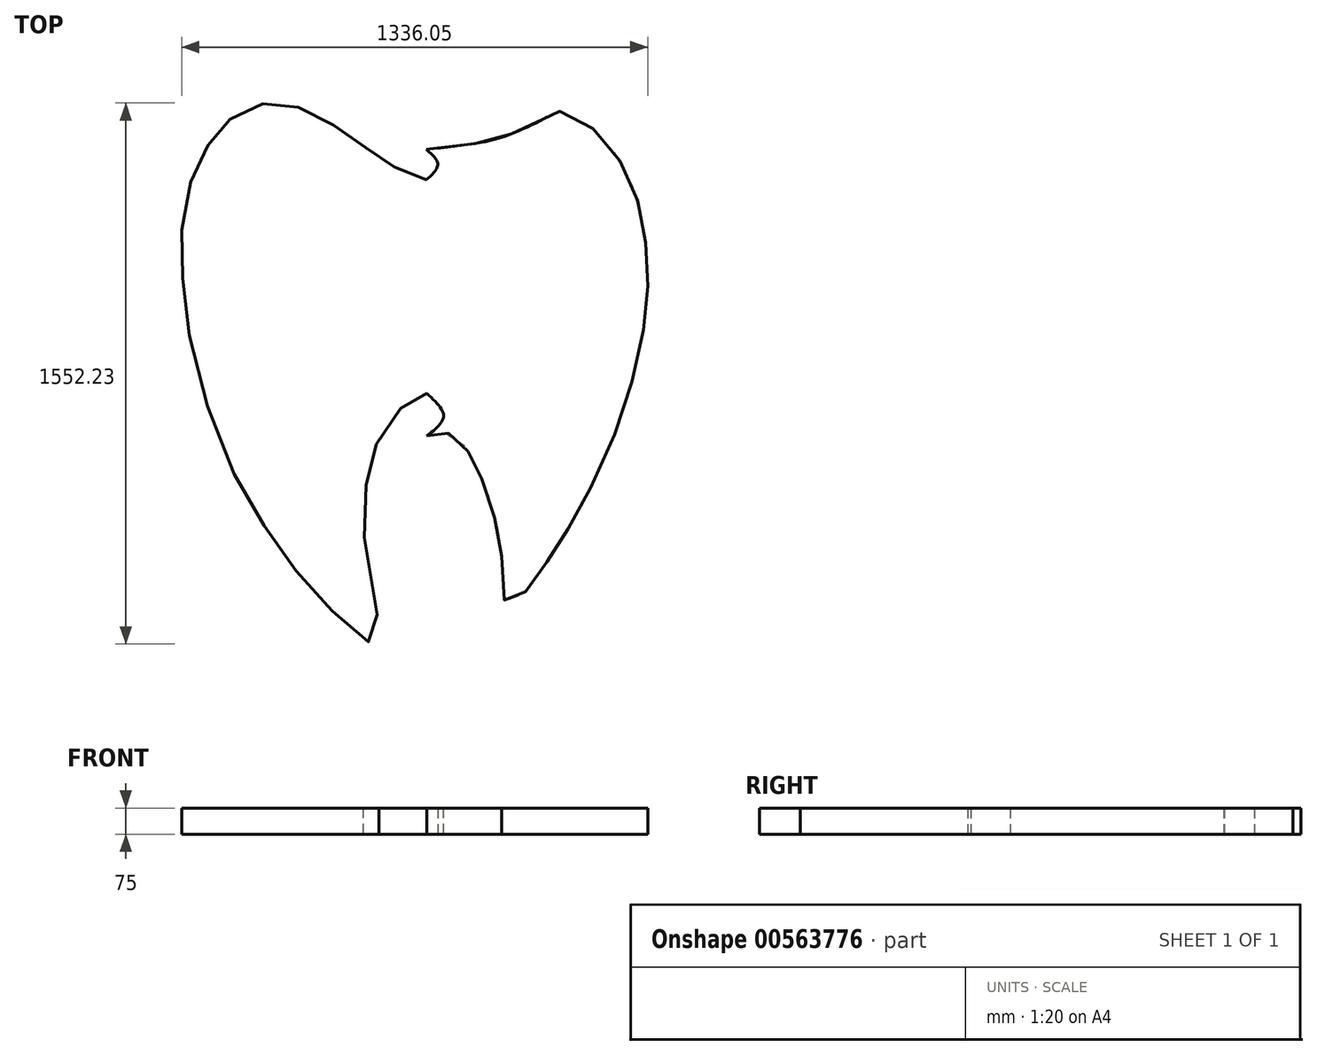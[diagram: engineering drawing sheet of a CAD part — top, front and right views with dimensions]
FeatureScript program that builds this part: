
annotation { "Feature Type Name" : "Feature", "Feature Type Description" : "" }
export const myFeature = defineFeature(function(context is Context, id is Id, definition is map)
    precondition{}
    {
        {
            var Q0;
            Q0=qCreatedBy(makeId("Top.planeOp"),FACE);
            var sketch = newSketch(context, id + "F0", { "sketchPlane" : qUnion([Q0])});
            skFitSpline(sketch, "E0", {"points": [v(131.96, -83.23) * mm, v(71.7, -58) * mm, v(9.47, -61.65) * mm, v(-42.11, -91.08) * mm, v(-114.72, -186.11) * mm, v(-148.68, -304.12) * mm, v(-156, -483.6) * mm, v(-121, -773.99) * mm, v(-175.45, -749.35) * mm, v(-306.38, -623.6) * mm, v(-428.24, -462.85) * mm, v(-551.4, -245.06) * mm, v(-659, 106.26) * mm, v(-679.74, 314.98) * mm, v(-674.56, 467.95) * mm, v(-629.18, 611.85) * mm, v(-586.4, 680.55) * mm, v(-526.77, 740.19) * mm, v(-445.1, 772.6) * mm, v(-358.24, 766.12) * mm, v(-270.09, 725.93) * mm, v(-172.86, 661.1) * mm, v(-115.82, 617.03) * mm, v(-31.55, 571.66) * mm, v(55.3, 550.92) * mm, v(199.2, 557.4) * mm, v(197.9, 557.4) * mm], "startDerivative": vector(-2057.54, 1113.53) * mm, "endDerivative": vector(-522.46, -16.62) * mm});
            skLineSegment(sketch, "E1", {"start": v(-24.8, 1210.26) * mm, "end": v(-24.8, -999.05) * mm, "construction": true});
            skLineSegment(sketch, "E2", {"start": v(199.2, 557.4) * mm, "end": v(131.96, -83.23) * mm});
            skSolve(sketch);
        }
        {
            var Q0;
            Q0=qCreatedBy(makeId("Top.planeOp"),FACE);
            var sketch = newSketch(context, id + "F1", { "sketchPlane" : qUnion([Q0])});
            skFitSpline(sketch, "E3", {"points": [v(21.78, -180.5) * mm, v(51.11, -172.25) * mm, v(86.86, -174.08) * mm, v(124.45, -203.42) * mm, v(155.61, -256.58) * mm, v(185.86, -320.75) * mm, v(222.53, -439) * mm, v(236.28, -543.5) * mm, v(249.12, -658.09) * mm, v(287.62, -644.34) * mm, v(329.78, -593.92) * mm, v(395.78, -496.75) * mm, v(449.87, -406.92) * mm, v(543.37, -218.08) * mm, v(613.04, -13.66) * mm, v(648.79, 165.09) * mm, v(654.29, 289.76) * mm, v(641.45, 425.43) * mm, v(609.37, 540.93) * mm, v(538.79, 659.18) * mm, v(455.37, 728.85) * mm, v(390.28, 751.76) * mm, v(382.03, 745.35) * mm, v(344.45, 722.43) * mm, v(268.37, 687.6) * mm, v(180.36, 661.93) * mm, v(19.95, 641.76) * mm], "startDerivative": vector(1286.51, 437.48) * mm, "endDerivative": vector(-3413.02, -338.45) * mm});
            skFitSpline(sketch, "E4", {"points": [v(21.78, -180.5) * mm, v(69.44, -123.53) * mm, v(21.78, -58.78) * mm], "startDerivative": vector(143.98, 113.6) * mm, "endDerivative": vector(-142.1, 129.73) * mm});
            skFitSpline(sketch, "E5", {"points": [v(19.95, 641.76) * mm, v(53.14, 598.3) * mm, v(21.78, 555.65) * mm], "startDerivative": vector(98.4, -86.29) * mm, "endDerivative": vector(-95.26, -85.94) * mm});
            skLineSegment(sketch, "E6", {"start": v(21.78, 555.65) * mm, "end": v(21.78, -58.78) * mm});
            skSolve(sketch);
        }
        {
            var Q0;
            {var subQ0=sQuery(id+"F0.wireOp",EDGE,"E2");Q0=makeQuery(id+"F0.imprint","IMPRINT",FACE,{"disambiguationData":[TD([[makeQuery(id+"F0.imprint","IMPRINT",EDGE,{"derivedFrom":subQ0}),-1.0]])]});}
            extrude(context, id + "F2", {"entities" : qUnion([Q0]), "depth" : 75 * mm, "offsetDistance" : 25 * mm});
        }
        {
            var Q0;
            Q0=makeQuery(id+"F1.imprint","IMPRINT",FACE,{"disambiguationData":[TD([[makeQuery(id+"F1.imprint","IMPRINT",EDGE,{"derivedFrom":sQuery(id+"F1.wireOp",EDGE,"E3")}),1.0]])]});
            extrude(context, id + "F3", {"entities" : qUnion([Q0]), "operationType" : NewBodyOperationType.ADD, "depth" : 75 * mm, "offsetDistance" : 25 * mm});
        }
    });
